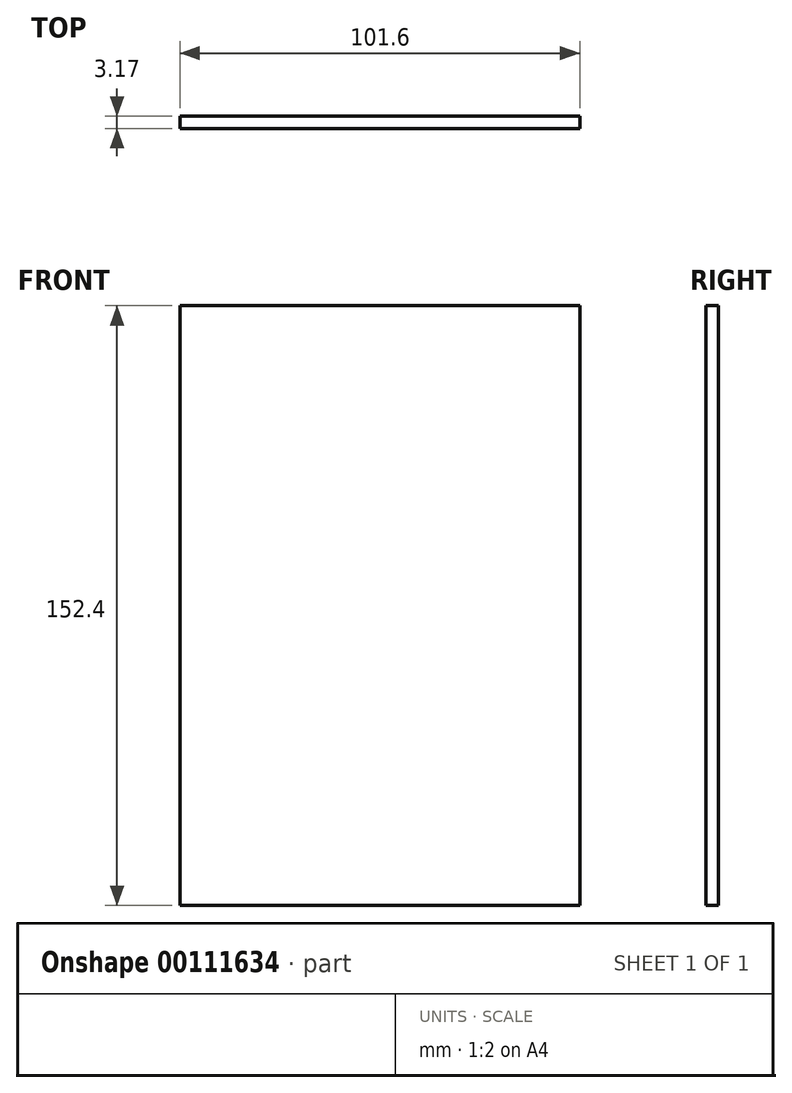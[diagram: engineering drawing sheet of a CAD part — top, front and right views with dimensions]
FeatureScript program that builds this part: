
annotation { "Feature Type Name" : "Feature", "Feature Type Description" : "" }
export const myFeature = defineFeature(function(context is Context, id is Id, definition is map)
    precondition{}
    {
        {
            var Q0;
            Q0=qCreatedBy(makeId("Front.planeOp"),FACE);
            var sketch = newSketch(context, id + "F0", { "sketchPlane" : qUnion([Q0])});
            skLineSegment(sketch, "E0.bottom", {"start": v(50.8, -76.2) * mm, "end": v(-50.8, -76.2) * mm});
            skLineSegment(sketch, "E0.top", {"start": v(50.8, 76.2) * mm, "end": v(-50.8, 76.2) * mm});
            skLineSegment(sketch, "E0.left", {"start": v(50.8, -76.2) * mm, "end": v(50.8, 76.2) * mm});
            skLineSegment(sketch, "E0.right", {"start": v(-50.8, -76.2) * mm, "end": v(-50.8, 76.2) * mm});
            skPoint(sketch, "E0.middle", {"position": v(0, 0) * mm});
            skSolve(sketch);
        }
        {
            var Q0;
            Q0 = qSketchRegion(id + "F0", true);
            extrude(context, id + "F1", {"entities" : qUnion([Q0]), "depth" : 3.17 * mm});
        }
    });
